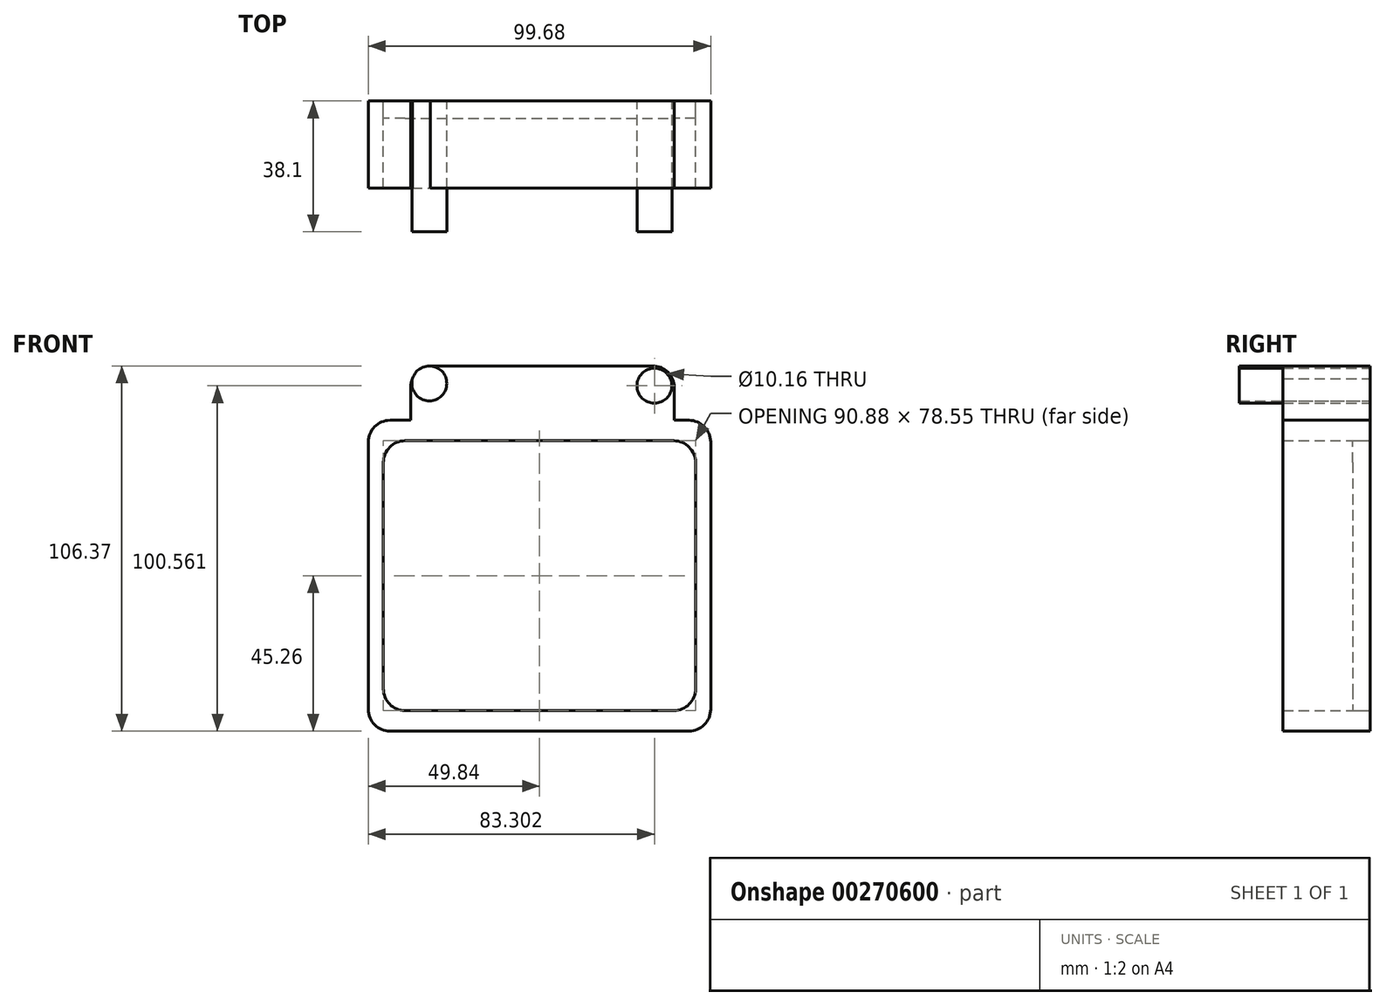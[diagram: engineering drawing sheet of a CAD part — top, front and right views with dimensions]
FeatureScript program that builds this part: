
annotation { "Feature Type Name" : "Feature", "Feature Type Description" : "" }
export const myFeature = defineFeature(function(context is Context, id is Id, definition is map)
    precondition{}
    {
        {
            var Q0;
            Q0=qCreatedBy(makeId("Front.planeOp"),FACE);
            var sketch = newSketch(context, id + "F0", { "sketchPlane" : qUnion([Q0])});
            skLineSegment(sketch, "E0.bottom", {"start": v(-43.5, 45.26) * mm, "end": v(43.5, 45.26) * mm});
            skLineSegment(sketch, "E0.top", {"start": v(-43.5, -45.26) * mm, "end": v(43.5, -45.26) * mm});
            skLineSegment(sketch, "E0.left", {"start": v(-49.84, 38.91) * mm, "end": v(-49.84, -38.91) * mm});
            skLineSegment(sketch, "E0.right", {"start": v(49.84, 38.91) * mm, "end": v(49.84, -38.91) * mm});
            skPoint(sketch, "E0.middle", {"position": v(0, 0) * mm});
            skLineSegment(sketch, "E1.bottom", {"start": v(-37.51, 39.27) * mm, "end": v(39.27, 39.27) * mm});
            skLineSegment(sketch, "E1.top", {"start": v(-31.16, 61.11) * mm, "end": v(32.92, 61.11) * mm});
            skLineSegment(sketch, "E1.left", {"start": v(-37.51, 39.27) * mm, "end": v(-37.51, 54.76) * mm});
            skLineSegment(sketch, "E1.right", {"start": v(39.27, 39.27) * mm, "end": v(39.27, 54.76) * mm});
            skLineSegment(sketch, "E2.bottom", {"start": v(-39.09, 39.27) * mm, "end": v(39.09, 39.27) * mm});
            skLineSegment(sketch, "E2.top", {"start": v(-39.09, -39.27) * mm, "end": v(39.09, -39.27) * mm});
            skLineSegment(sketch, "E2.left", {"start": v(-45.44, 32.92) * mm, "end": v(-45.44, -32.92) * mm});
            skLineSegment(sketch, "E2.right", {"start": v(45.44, 32.92) * mm, "end": v(45.44, -32.92) * mm});
            skCircle(sketch, "E3", {"center": v(-32.05, 56) * mm, "radius": 5.08 * mm});
            skCircle(sketch, "E4", {"center": v(33.46, 55.3) * mm, "radius": 5.08 * mm});
            skPoint(sketch, "E5.visualSharp", {"position": v(-45.44, 39.27) * mm});
            skArc(sketch, "E5.filletArc", {"start": v(-39.09, 39.27) * mm, "mid": v(-43.58, 37.41) * mm, "end": v(-45.44, 32.92) * mm});
            skPoint(sketch, "E6.visualSharp", {"position": v(45.44, 39.27) * mm});
            skArc(sketch, "E6.filletArc", {"start": v(45.44, 32.92) * mm, "mid": v(43.58, 37.41) * mm, "end": v(39.09, 39.27) * mm});
            skPoint(sketch, "E7.visualSharp", {"position": v(45.44, -39.27) * mm});
            skArc(sketch, "E7.filletArc", {"start": v(39.09, -39.27) * mm, "mid": v(43.58, -37.41) * mm, "end": v(45.44, -32.92) * mm});
            skPoint(sketch, "E8.visualSharp", {"position": v(-45.44, -39.27) * mm});
            skArc(sketch, "E8.filletArc", {"start": v(-45.44, -32.92) * mm, "mid": v(-43.58, -37.41) * mm, "end": v(-39.09, -39.27) * mm});
            skPoint(sketch, "E9.visualSharp", {"position": v(-49.84, -45.26) * mm});
            skArc(sketch, "E9.filletArc", {"start": v(-49.84, -38.91) * mm, "mid": v(-47.98, -43.4) * mm, "end": v(-43.5, -45.26) * mm});
            skPoint(sketch, "E10.visualSharp", {"position": v(49.84, -45.26) * mm});
            skArc(sketch, "E10.filletArc", {"start": v(43.5, -45.26) * mm, "mid": v(47.98, -43.4) * mm, "end": v(49.84, -38.91) * mm});
            skPoint(sketch, "E11.visualSharp", {"position": v(49.84, 45.26) * mm});
            skArc(sketch, "E11.filletArc", {"start": v(49.84, 38.91) * mm, "mid": v(47.98, 43.4) * mm, "end": v(43.5, 45.26) * mm});
            skPoint(sketch, "E12.visualSharp", {"position": v(-49.84, 45.26) * mm});
            skArc(sketch, "E12.filletArc", {"start": v(-43.5, 45.26) * mm, "mid": v(-47.98, 43.4) * mm, "end": v(-49.84, 38.91) * mm});
            skPoint(sketch, "E13.visualSharp", {"position": v(-37.51, 61.11) * mm});
            skArc(sketch, "E13.filletArc", {"start": v(-31.16, 61.11) * mm, "mid": v(-35.65, 59.25) * mm, "end": v(-37.51, 54.76) * mm});
            skPoint(sketch, "E14.visualSharp", {"position": v(39.27, 61.11) * mm});
            skArc(sketch, "E14.filletArc", {"start": v(39.27, 54.76) * mm, "mid": v(37.41, 59.25) * mm, "end": v(32.92, 61.11) * mm});
            skSolve(sketch);
        }
        {
            var Q0;
            Q0=makeQuery(id+"F0.imprint","IMPRINT",FACE,{"disambiguationData":[TD([[makeQuery(id+"F0.imprint","IMPRINT",EDGE,{"derivedFrom":sQuery(id+"F0.wireOp",EDGE,"E2.top")}),1.0]])]});
            extrude(context, id + "F1", {"entities" : qUnion([Q0]), "depth" : 5.08 * mm});
        }
        {
            var Q0;
            Q0=makeQuery(id+"F0.imprint","IMPRINT",FACE,{"disambiguationData":[TD([[makeQuery(id+"F0.imprint","IMPRINT",EDGE,{"derivedFrom":sQuery(id+"F0.wireOp",EDGE,"E0.top")}),1.0]])]});
            var Q1;
            {var subQ0=sQuery(id+"F0.wireOp",EDGE,"E1.left");var subQ1=sQuery(id+"F0.wireOp",EDGE,"E0.bottom");var subQ2=makeQuery(id+"F0.imprint","INTERSECT",VERTEX,{"derivedFrom":[subQ1,subQ0]});Q1=makeQuery(id+"F0.imprint","IMPRINT",FACE,{"disambiguationData":[TD([[makeQuery(id+"F0.imprint","IMPRINT",EDGE,{"disambiguationData":[TD([[subQ2,-1.0]])],"derivedFrom":subQ1}),-1.0]])]});}
            var Q2;
            {var subQ1=sQuery(id+"F0.wireOp",EDGE,"E1.top");Q2=makeQuery(id+"F0.imprint","IMPRINT",FACE,{"disambiguationData":[TD([[makeQuery(id+"F0.imprint","IMPRINT",EDGE,{"derivedFrom":subQ1}),-1.0]])]});}
            extrude(context, id + "F2", {"entities" : qUnion([Q0, Q1, Q2]), "depth" : 25.4 * mm});
        }
        {
            var Q0;
            Q0=makeQuery(id+"F0.imprint","IMPRINT",FACE,{"disambiguationData":[TD([[makeQuery(id+"F0.imprint","IMPRINT",EDGE,{"derivedFrom":sQuery(id+"F0.wireOp",EDGE,"E3")}),1.0]])]});
            var Q1;
            Q1=makeQuery(id+"F0.imprint","IMPRINT",FACE,{"disambiguationData":[TD([[makeQuery(id+"F0.imprint","IMPRINT",EDGE,{"derivedFrom":sQuery(id+"F0.wireOp",EDGE,"E4")}),1.0]])]});
            extrude(context, id + "F3", {"entities" : qUnion([Q0, Q1]), "depth" : 38.1 * mm});
        }
    });
